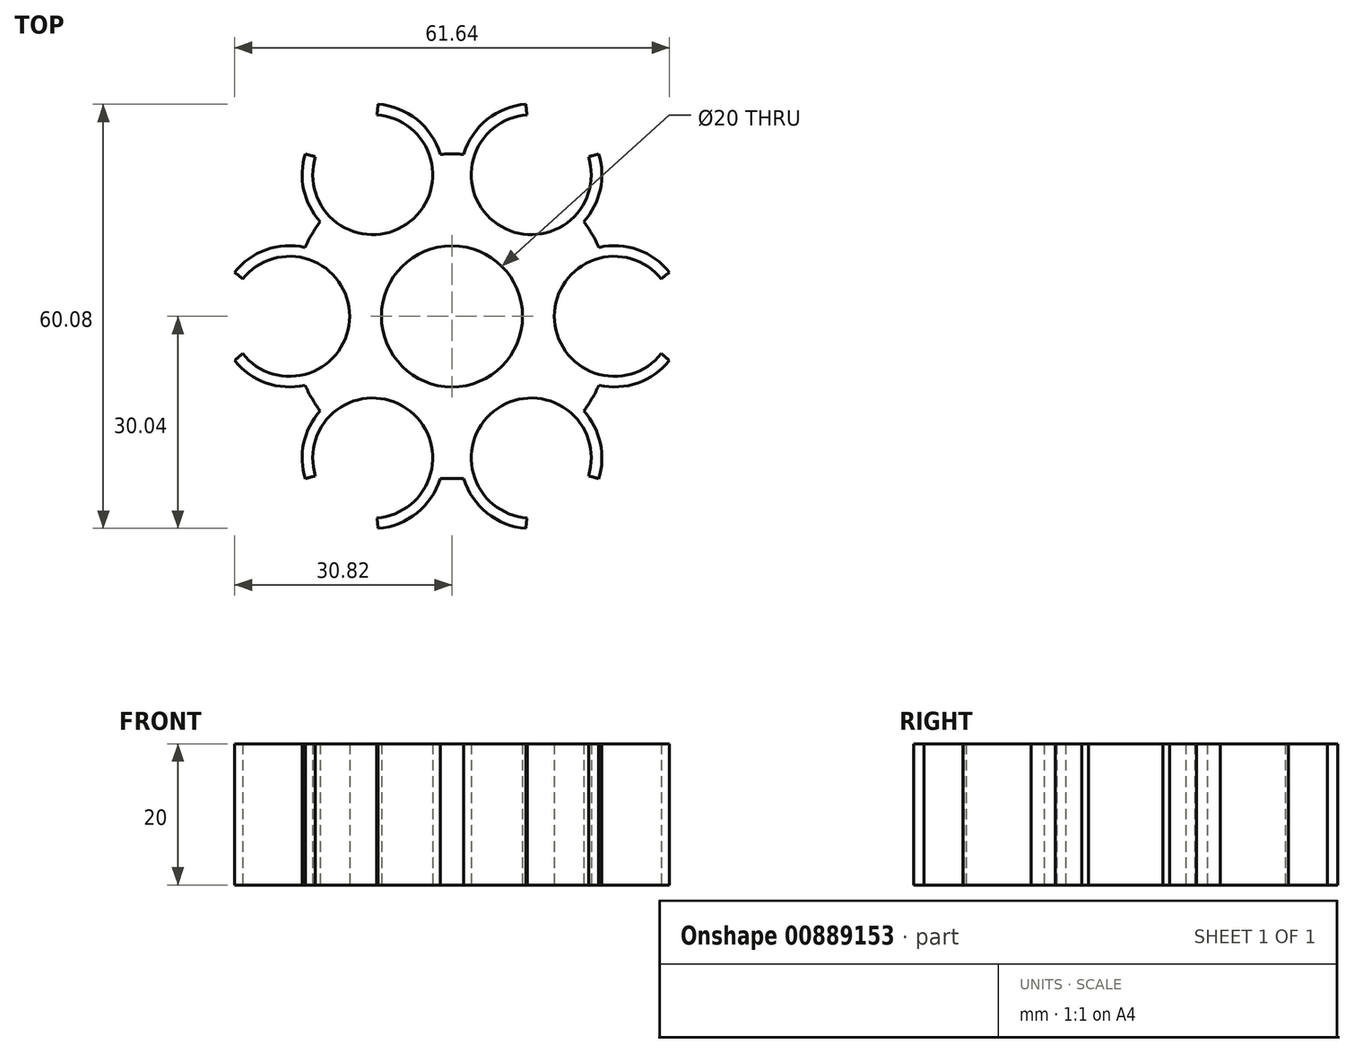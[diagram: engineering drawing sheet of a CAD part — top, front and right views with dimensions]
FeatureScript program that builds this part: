
annotation { "Feature Type Name" : "Feature", "Feature Type Description" : "" }
export const myFeature = defineFeature(function(context is Context, id is Id, definition is map)
    precondition{}
    {
        {
            var Q0;
            Q0=qCreatedBy(makeId("Top.planeOp"),FACE);
            var sketch = newSketch(context, id + "F0", { "sketchPlane" : qUnion([Q0])});
            skArc(sketch, "E0", {"start": v(14.82, -2.31) * mm, "mid": v(21.34, -8.34) * mm, "end": v(29.67, -5.27) * mm});
            skArc(sketch, "E1", {"start": v(5.22, -14.06) * mm, "mid": v(3.27, -23.05) * mm, "end": v(10.64, -28.55) * mm});
            skArc(sketch, "E2.MirrorC", {"start": v(5.22, 14.06) * mm, "mid": v(3.27, 23.05) * mm, "end": v(10.64, 28.55) * mm});
            skArc(sketch, "E3.MirrorC", {"start": v(-5.22, 14.06) * mm, "mid": v(-3.27, 23.05) * mm, "end": v(-10.64, 28.55) * mm});
            skArc(sketch, "E4.MirrorC", {"start": v(-14.82, -2.31) * mm, "mid": v(-21.34, -8.34) * mm, "end": v(-29.67, -5.27) * mm});
            skArc(sketch, "E5.MirrorC", {"start": v(-5.22, -14.06) * mm, "mid": v(-3.27, -23.05) * mm, "end": v(-10.64, -28.55) * mm});
            skPoint(sketch, "E6.middle", {"position": v(0, 0) * mm});
            skArc(sketch, "E7", {"start": v(-18.69, 13.4) * mm, "mid": v(-19.84, 11.63) * mm, "end": v(-20.83, 9.76) * mm});
            skArc(sketch, "E8.trimOffspring", {"start": v(3.18, 22.78) * mm, "mid": v(0.77, 22.99) * mm, "end": v(-1.65, 22.94) * mm});
            skArc(sketch, "E9.trimOffspring", {"start": v(-20.83, -9.76) * mm, "mid": v(-19.84, -11.63) * mm, "end": v(-18.69, -13.4) * mm});
            skArc(sketch, "E10.trimOffspring", {"start": v(-1.65, -22.94) * mm, "mid": v(0, -23) * mm, "end": v(1.65, -22.94) * mm});
            skArc(sketch, "E11.trimOffspring", {"start": v(18.69, -13.4) * mm, "mid": v(19.84, -11.63) * mm, "end": v(20.83, -9.76) * mm});
            skArc(sketch, "E12.trimOffspring", {"start": v(20.83, 9.76) * mm, "mid": v(19.84, 11.63) * mm, "end": v(18.69, 13.4) * mm});
            skArc(sketch, "E13", {"start": v(20.78, -23.04) * mm, "mid": v(20.07, -22.8) * mm, "end": v(19.34, -22.62) * mm});
            skArc(sketch, "E14.MirrorC", {"start": v(-20.78, -23.04) * mm, "mid": v(-20.07, -22.8) * mm, "end": v(-19.34, -22.62) * mm});
            skArc(sketch, "E15.MirrorC", {"start": v(-10.64, 28.55) * mm, "mid": v(-10.53, 29.3) * mm, "end": v(-10.5, 30.04) * mm});
            skArc(sketch, "E16.MirrorC", {"start": v(20.78, 23.04) * mm, "mid": v(20.07, 22.8) * mm, "end": v(19.34, 22.62) * mm});
            skArc(sketch, "E17", {"start": v(30.82, 6.23) * mm, "mid": v(30.22, 5.78) * mm, "end": v(29.67, 5.27) * mm});
            skArc(sketch, "E18", {"start": v(30.82, 6.23) * mm, "mid": v(26.33, 9.43) * mm, "end": v(20.83, 9.76) * mm});
            skArc(sketch, "E19", {"start": v(1.65, -22.94) * mm, "mid": v(4.97, -27.87) * mm, "end": v(10.5, -30.04) * mm});
            skArc(sketch, "E20.MirrorC", {"start": v(-20.78, -23.04) * mm, "mid": v(-21, -17.94) * mm, "end": v(-18.69, -13.4) * mm});
            skArc(sketch, "E21.MirrorC", {"start": v(-30.82, 6.23) * mm, "mid": v(-26.33, 9.43) * mm, "end": v(-20.83, 9.76) * mm});
            skArc(sketch, "E22.MirrorC", {"start": v(-20.78, 23.04) * mm, "mid": v(-21, 17.94) * mm, "end": v(-18.69, 13.4) * mm});
            skArc(sketch, "E23.MirrorC", {"start": v(20.78, 23.04) * mm, "mid": v(21, 17.94) * mm, "end": v(18.69, 13.4) * mm});
            skArc(sketch, "E24.trimOffspring", {"start": v(-19.34, 22.62) * mm, "mid": v(-17.45, 14.27) * mm, "end": v(-9.26, 11.8) * mm});
            skArc(sketch, "E25.trimOffspring", {"start": v(-20.78, 23.04) * mm, "mid": v(-20.07, 22.8) * mm, "end": v(-19.34, 22.62) * mm});
            skArc(sketch, "E26.MirrorC", {"start": v(-29.67, -5.27) * mm, "mid": v(-30.22, -5.78) * mm, "end": v(-30.82, -6.23) * mm});
            skArc(sketch, "E27.trimOffspring", {"start": v(-29.67, 5.27) * mm, "mid": v(-21.34, 8.34) * mm, "end": v(-14.82, 2.31) * mm});
            skArc(sketch, "E28.trimOffspring", {"start": v(-30.82, 6.23) * mm, "mid": v(-30.22, 5.78) * mm, "end": v(-29.67, 5.27) * mm});
            skArc(sketch, "E29.trimOffspring", {"start": v(10.64, 28.55) * mm, "mid": v(10.53, 29.3) * mm, "end": v(10.5, 30.04) * mm});
            skArc(sketch, "E30.trimOffspring", {"start": v(19.34, 22.62) * mm, "mid": v(17.45, 14.27) * mm, "end": v(9.26, 11.8) * mm});
            skArc(sketch, "E31.trimOffspring", {"start": v(-1.65, 22.94) * mm, "mid": v(-4.97, 27.87) * mm, "end": v(-10.5, 30.04) * mm});
            skArc(sketch, "E32.trimOffspring", {"start": v(1.65, 22.94) * mm, "mid": v(4.97, 27.87) * mm, "end": v(10.5, 30.04) * mm});
            skArc(sketch, "E33.trimOffspring", {"start": v(-20.83, -9.76) * mm, "mid": v(-26.33, -9.43) * mm, "end": v(-30.82, -6.23) * mm});
            skArc(sketch, "E34.trimOffspring", {"start": v(29.67, 5.27) * mm, "mid": v(21.34, 8.34) * mm, "end": v(14.82, 2.31) * mm});
            skArc(sketch, "E35.trimOffspring", {"start": v(29.67, -5.27) * mm, "mid": v(30.22, -5.78) * mm, "end": v(30.82, -6.23) * mm});
            skArc(sketch, "E36.trimOffspring", {"start": v(20.83, -9.76) * mm, "mid": v(26.33, -9.43) * mm, "end": v(30.82, -6.23) * mm});
            skArc(sketch, "E37.trimOffspring", {"start": v(-19.34, -22.62) * mm, "mid": v(-17.45, -14.27) * mm, "end": v(-9.26, -11.8) * mm});
            skArc(sketch, "E38.trimOffspring", {"start": v(-1.65, -22.94) * mm, "mid": v(-4.97, -27.87) * mm, "end": v(-10.5, -30.04) * mm});
            skArc(sketch, "E39.trimOffspring", {"start": v(20.78, -23.04) * mm, "mid": v(21, -17.94) * mm, "end": v(18.69, -13.4) * mm});
            skArc(sketch, "E40.trimOffspring", {"start": v(19.34, -22.62) * mm, "mid": v(17.45, -14.27) * mm, "end": v(9.26, -11.8) * mm});
            skArc(sketch, "E41.trimOffspring", {"start": v(10.64, -28.55) * mm, "mid": v(10.53, -29.3) * mm, "end": v(10.5, -30.04) * mm});
            skArc(sketch, "E42.trimOffspring", {"start": v(-10.64, -28.55) * mm, "mid": v(-10.53, -29.3) * mm, "end": v(-10.5, -30.04) * mm});
            skArc(sketch, "E43", {"start": v(-29.67, -5.27) * mm, "mid": v(-14.5, 0) * mm, "end": v(-29.67, 5.27) * mm});
            skArc(sketch, "E44", {"start": v(-19.34, 22.62) * mm, "mid": v(-6.45, 13.05) * mm, "end": v(-10.64, 28.55) * mm});
            skArc(sketch, "E45", {"start": v(10.64, 28.55) * mm, "mid": v(6.45, 13.05) * mm, "end": v(19.34, 22.62) * mm});
            skArc(sketch, "E46", {"start": v(29.67, 5.27) * mm, "mid": v(14.5, 0) * mm, "end": v(29.67, -5.27) * mm});
            skArc(sketch, "E47", {"start": v(19.34, -22.62) * mm, "mid": v(6.45, -13.05) * mm, "end": v(10.64, -28.55) * mm});
            skArc(sketch, "E48", {"start": v(-10.64, -28.55) * mm, "mid": v(-6.45, -13.05) * mm, "end": v(-19.34, -22.62) * mm});
            skCircle(sketch, "E49", {"center": v(0, 0) * mm, "radius": 10 * mm});
            skSolve(sketch);
        }
        {
            var Q0;
            Q0 = qSketchRegion(id + "F0", true);
            extrude(context, id + "F1", {"entities" : qUnion([Q0]), "depth" : 20 * mm, "offsetDistance" : 25 * mm});
        }
    });
